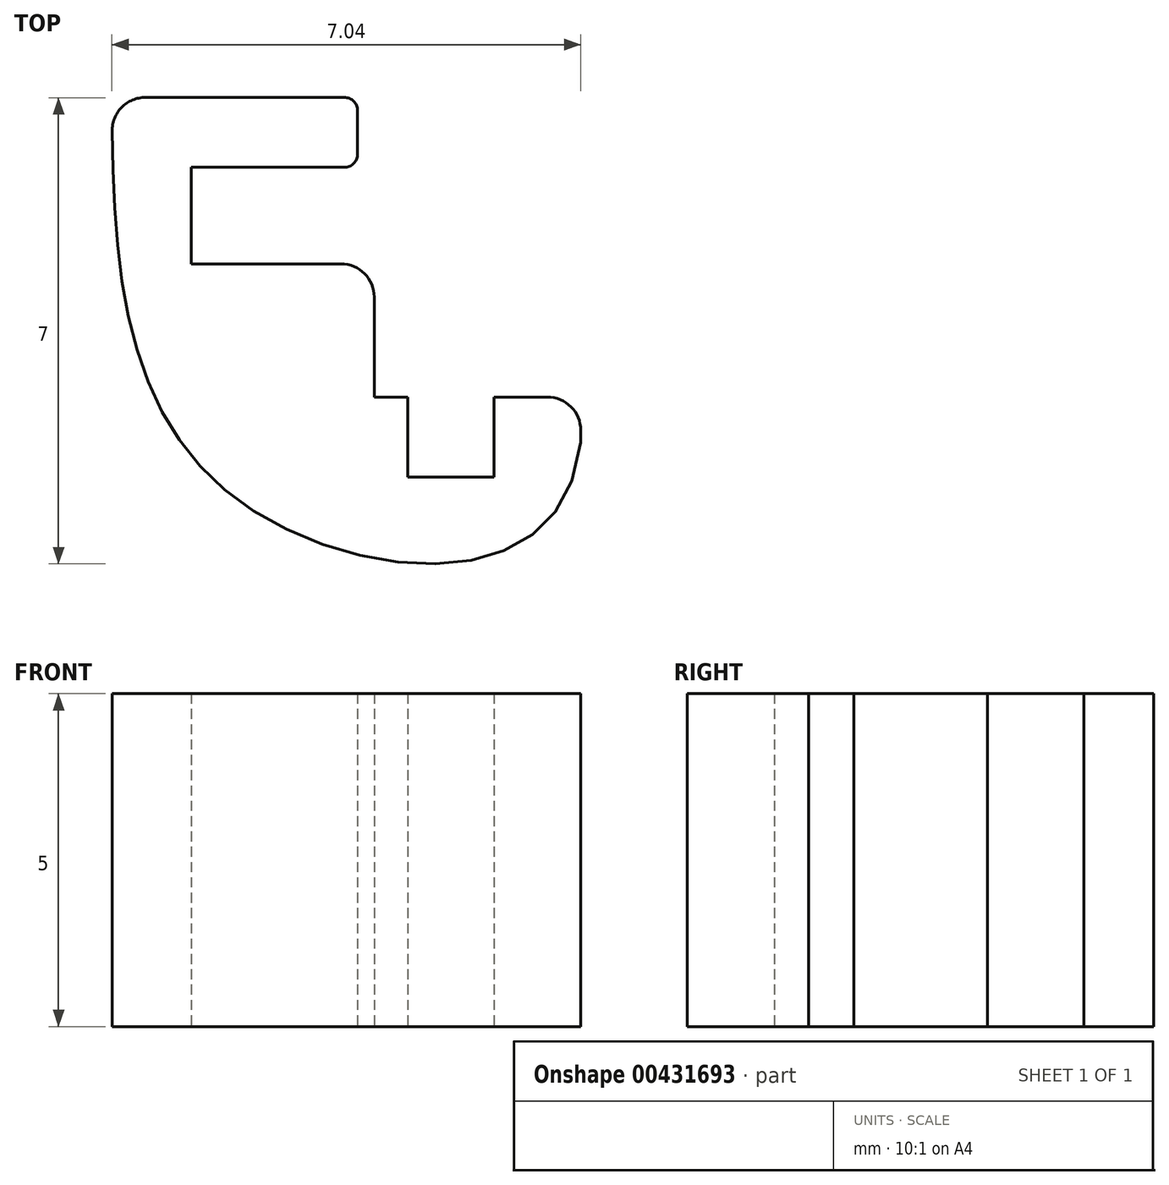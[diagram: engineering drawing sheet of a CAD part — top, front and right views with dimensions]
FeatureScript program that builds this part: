
annotation { "Feature Type Name" : "Feature", "Feature Type Description" : "" }
export const myFeature = defineFeature(function(context is Context, id is Id, definition is map)
    precondition{}
    {
        {
            var Q0;
            Q0=qCreatedBy(makeId("Top.planeOp"),FACE);
            var sketch = newSketch(context, id + "F0", { "sketchPlane" : qUnion([Q0])});
            skLineSegment(sketch, "E0", {"start": v(-2.96, -5.26) * mm, "end": v(-3.76, -5.26) * mm});
            skLineSegment(sketch, "E1", {"start": v(-3.76, -5.26) * mm, "end": v(-3.76, -6.46) * mm});
            skLineSegment(sketch, "E2", {"start": v(-3.76, -6.46) * mm, "end": v(-5.06, -6.46) * mm});
            skLineSegment(sketch, "E3", {"start": v(-5.06, -6.46) * mm, "end": v(-5.06, -5.26) * mm});
            skLineSegment(sketch, "E4", {"start": v(-6.06, -3.26) * mm, "end": v(-8.31, -3.26) * mm});
            skLineSegment(sketch, "E5", {"start": v(-8.31, -3.26) * mm, "end": v(-8.31, -0.76) * mm});
            skLineSegment(sketch, "E6", {"start": v(-8.31, -0.76) * mm, "end": v(-9, -0.76) * mm});
            skLineSegment(sketch, "E7", {"start": v(-2.46, -5.76) * mm, "end": v(-2.46, -5.94) * mm});
            skFitSpline(sketch, "E8", {"points": [v(-9.5, -0.76) * mm, v(-7.48, -6.9) * mm, v(-2.46, -5.94) * mm], "startDerivative": vector(0.02, -14.08) * mm, "endDerivative": vector(1.6, 15.37) * mm});
            skLineSegment(sketch, "E9.bottom", {"start": v(-8.31, -0.76) * mm, "end": v(-6.01, -0.76) * mm});
            skLineSegment(sketch, "E9.top", {"start": v(-8.31, -1.8) * mm, "end": v(-6.01, -1.8) * mm});
            skLineSegment(sketch, "E9.left", {"start": v(-8.31, -0.76) * mm, "end": v(-8.31, -1.8) * mm});
            skLineSegment(sketch, "E9.right", {"start": v(-5.81, -0.96) * mm, "end": v(-5.81, -1.6) * mm});
            skLineSegment(sketch, "E10", {"start": v(-5.06, -5.26) * mm, "end": v(-5.56, -5.26) * mm});
            skLineSegment(sketch, "E11", {"start": v(-5.56, -5.26) * mm, "end": v(-5.56, -3.76) * mm});
            skPoint(sketch, "E12.visualSharp", {"position": v(-5.56, -3.26) * mm});
            skArc(sketch, "E12.filletArc", {"start": v(-5.56, -3.76) * mm, "mid": v(-5.7, -3.4) * mm, "end": v(-6.06, -3.26) * mm});
            skArc(sketch, "E13.filletArc", {"start": v(-9, -0.76) * mm, "mid": v(-9.35, -0.9) * mm, "end": v(-9.5, -1.26) * mm});
            skPoint(sketch, "E14.visualSharp", {"position": v(-5.81, -0.76) * mm});
            skArc(sketch, "E14.filletArc", {"start": v(-5.81, -0.96) * mm, "mid": v(-5.87, -0.81) * mm, "end": v(-6.01, -0.76) * mm});
            skPoint(sketch, "E15.visualSharp", {"position": v(-5.81, -1.8) * mm});
            skArc(sketch, "E15.filletArc", {"start": v(-6.01, -1.8) * mm, "mid": v(-5.87, -1.75) * mm, "end": v(-5.81, -1.6) * mm});
            skPoint(sketch, "E16.visualSharp", {"position": v(-2.46, -5.26) * mm});
            skArc(sketch, "E16.filletArc", {"start": v(-2.46, -5.76) * mm, "mid": v(-2.6, -5.4) * mm, "end": v(-2.96, -5.26) * mm});
            skSolve(sketch);
        }
        {
            var Q0;
            Q0=makeQuery(id+"F0.imprint","IMPRINT",FACE,{"disambiguationData":[TD([[makeQuery(id+"F0.imprint","IMPRINT",EDGE,{"derivedFrom":sQuery(id+"F0.wireOp",EDGE,"E0")}),1.0]])]});
            var Q1;
            Q1=makeQuery(id+"F0.imprint","IMPRINT",FACE,{"disambiguationData":[TD([[makeQuery(id+"F0.imprint","IMPRINT",EDGE,{"derivedFrom":sQuery(id+"F0.wireOp",EDGE,"E9.bottom")}),-1.0]])]});
            extrude(context, id + "F1", {"entities" : qUnion([Q0, Q1]), "depth" : 5 * mm});
        }
    });
